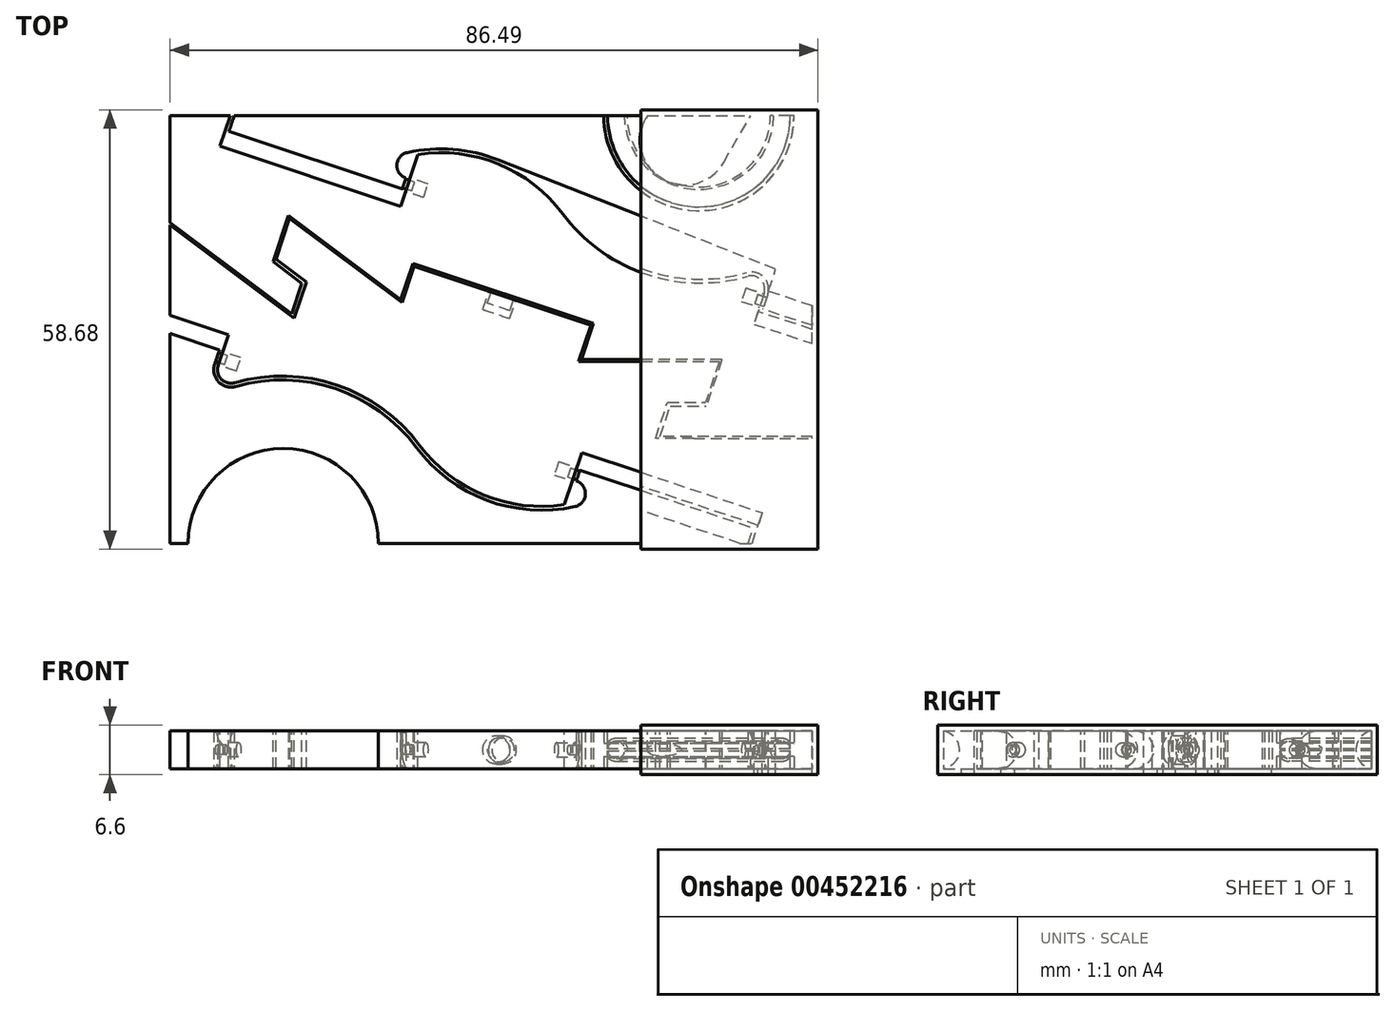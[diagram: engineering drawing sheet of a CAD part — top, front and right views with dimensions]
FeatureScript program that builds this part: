
annotation { "Feature Type Name" : "Feature", "Feature Type Description" : "" }
export const myFeature = defineFeature(function(context is Context, id is Id, definition is map)
    precondition{}
    {
        {
            var Q0;
            Q0=qCreatedBy(makeId("Top.planeOp"),FACE);
            cPlane(context, id + "F0", {"entities" : qUnion([Q0]), "cplaneType" : CPlaneType.OFFSET, "offset" : 2.54 * mm, "width" : 152.4 * mm, "height" : 152.4 * mm});
        }
        {
            var Q0;
            Q0=qCreatedBy(makeId("Top.planeOp"),FACE);
            var sketch = newSketch(context, id + "F1", { "sketchPlane" : qUnion([Q0])});
            skLineSegment(sketch, "E0", {"start": v(0, 0) * mm, "end": v(0, 28.58) * mm});
            skLineSegment(sketch, "E1", {"start": v(0, 0) * mm, "end": v(85.73, 0) * mm, "construction": true});
            skLineSegment(sketch, "E2", {"start": v(0, 28.58) * mm, "end": v(85.73, 0) * mm, "construction": true});
            skLineSegment(sketch, "E3", {"start": v(0, 28.58) * mm, "end": v(8.03, 28.58) * mm});
            skLineSegment(sketch, "E4", {"start": v(8.03, 28.58) * mm, "end": v(7.23, 26.17) * mm});
            skLineSegment(sketch, "E5", {"start": v(7.23, 26.17) * mm, "end": v(31.33, 18.13) * mm});
            skLineSegment(sketch, "E6", {"start": v(31.33, 18.13) * mm, "end": v(32.13, 20.54) * mm});
            skLineSegment(sketch, "E7", {"start": v(32.13, 20.54) * mm, "end": v(31.65, 20.7) * mm});
            skArc(sketch, "E8", {"start": v(31.78, 23.15) * mm, "mid": v(30.78, 21.98) * mm, "end": v(31.65, 20.7) * mm});
            skArc(sketch, "E9", {"start": v(52.44, 15.43) * mm, "mid": v(43.25, 22.34) * mm, "end": v(31.78, 23.15) * mm});
            skArc(sketch, "E10", {"start": v(52.44, 15.43) * mm, "mid": v(63.47, 7.42) * mm, "end": v(77.1, 7.11) * mm});
            skArc(sketch, "E11", {"start": v(79.3, 4.82) * mm, "mid": v(78.9, 6.63) * mm, "end": v(77.1, 7.11) * mm});
            skLineSegment(sketch, "E12", {"start": v(79.3, 4.82) * mm, "end": v(78.5, 2.4) * mm});
            skLineSegment(sketch, "E13", {"start": v(78.5, 2.4) * mm, "end": v(85.73, 0) * mm});
            skLineSegment(sketch, "E14", {"start": v(0, 0) * mm, "end": v(0, -28.58) * mm, "construction": true});
            skLineSegment(sketch, "E15", {"start": v(0, -28.58) * mm, "end": v(85.73, -28.58) * mm, "construction": true});
            skLineSegment(sketch, "E16", {"start": v(0, 14.29) * mm, "end": v(85.73, -14.29) * mm, "construction": true});
            skLineSegment(sketch, "E17", {"start": v(85.73, 0) * mm, "end": v(85.73, -14.29) * mm});
            skLineSegment(sketch, "E18", {"start": v(85.73, -14.29) * mm, "end": v(70.23, -14.29) * mm});
            skLineSegment(sketch, "E19", {"start": v(73.65, -4.02) * mm, "end": v(54.91, -4.02) * mm});
            skLineSegment(sketch, "E20", {"start": v(54.91, -4.02) * mm, "end": v(56.52, 0.8) * mm});
            skLineSegment(sketch, "E21", {"start": v(56.52, 0.8) * mm, "end": v(32.42, 8.84) * mm});
            skLineSegment(sketch, "E22", {"start": v(32.42, 8.84) * mm, "end": v(30.81, 4.02) * mm});
            skLineSegment(sketch, "E23", {"start": v(30.81, 4.02) * mm, "end": v(15.82, 15.26) * mm});
            skLineSegment(sketch, "E24", {"start": v(12.4, 5) * mm, "end": v(0, 14.29) * mm});
            skLineSegment(sketch, "E25", {"start": v(15.82, 15.26) * mm, "end": v(12.4, 5) * mm});
            skLineSegment(sketch, "E26", {"start": v(73.65, -4.02) * mm, "end": v(70.23, -14.29) * mm});
            skSolve(sketch);
        }
        {
            var Q0;
            Q0=qCreatedBy(makeId("Top.planeOp"),FACE);
            var sketch = newSketch(context, id + "F2", { "sketchPlane" : qUnion([Q0])});
            skLineSegment(sketch, "E27", {"start": v(85.73, 0) * mm, "end": v(85.73, -28.58) * mm, "construction": true});
            skLineSegment(sketch, "E28", {"start": v(85.73, 0) * mm, "end": v(0, 0) * mm, "construction": true});
            skLineSegment(sketch, "E29", {"start": v(85.73, -28.58) * mm, "end": v(0, 0) * mm, "construction": true});
            skLineSegment(sketch, "E30", {"start": v(85.73, -28.58) * mm, "end": v(77.7, -28.58) * mm});
            skLineSegment(sketch, "E31", {"start": v(77.7, -28.58) * mm, "end": v(78.5, -26.17) * mm});
            skLineSegment(sketch, "E32", {"start": v(78.5, -26.17) * mm, "end": v(54.4, -18.13) * mm});
            skLineSegment(sketch, "E33", {"start": v(54.4, -18.13) * mm, "end": v(53.6, -20.54) * mm});
            skLineSegment(sketch, "E34", {"start": v(53.6, -20.54) * mm, "end": v(54.08, -20.7) * mm});
            skArc(sketch, "E35", {"start": v(53.95, -23.15) * mm, "mid": v(54.94, -21.98) * mm, "end": v(54.08, -20.7) * mm});
            skArc(sketch, "E36", {"start": v(33.29, -15.43) * mm, "mid": v(42.48, -22.34) * mm, "end": v(53.95, -23.15) * mm});
            skArc(sketch, "E37", {"start": v(33.29, -15.43) * mm, "mid": v(22.26, -7.42) * mm, "end": v(8.62, -7.11) * mm});
            skArc(sketch, "E38", {"start": v(6.43, -4.82) * mm, "mid": v(6.83, -6.63) * mm, "end": v(8.62, -7.11) * mm});
            skLineSegment(sketch, "E39", {"start": v(6.43, -4.82) * mm, "end": v(7.23, -2.4) * mm});
            skLineSegment(sketch, "E40", {"start": v(7.23, -2.4) * mm, "end": v(0, 0) * mm});
            skLineSegment(sketch, "E41", {"start": v(85.73, 0) * mm, "end": v(85.73, 28.58) * mm, "construction": true});
            skLineSegment(sketch, "E42", {"start": v(85.73, 28.58) * mm, "end": v(0, 28.58) * mm, "construction": true});
            skLineSegment(sketch, "E43", {"start": v(85.73, -14.29) * mm, "end": v(0, 14.29) * mm, "construction": true});
            skLineSegment(sketch, "E44", {"start": v(0, 0) * mm, "end": v(0, 14.29) * mm, "construction": true});
            skLineSegment(sketch, "E45", {"start": v(0, 0) * mm, "end": v(0, 13.97) * mm});
            skLineSegment(sketch, "E46", {"start": v(12.53, 4.58) * mm, "end": v(15.95, 14.85) * mm});
            skLineSegment(sketch, "E47", {"start": v(15.95, 14.85) * mm, "end": v(30.94, 3.6) * mm});
            skLineSegment(sketch, "E48", {"start": v(30.94, 3.6) * mm, "end": v(32.55, 8.42) * mm});
            skLineSegment(sketch, "E49", {"start": v(32.55, 8.42) * mm, "end": v(56.16, 0.55) * mm});
            skLineSegment(sketch, "E50", {"start": v(56.16, 0.55) * mm, "end": v(54.56, -4.27) * mm});
            skLineSegment(sketch, "E51", {"start": v(54.56, -4.27) * mm, "end": v(73.3, -4.27) * mm});
            skLineSegment(sketch, "E52", {"start": v(73.3, -4.27) * mm, "end": v(69.88, -14.54) * mm});
            skLineSegment(sketch, "E53", {"start": v(69.88, -14.54) * mm, "end": v(85.73, -14.54) * mm});
            skLineSegment(sketch, "E54", {"start": v(0, 13.97) * mm, "end": v(12.53, 4.58) * mm});
            skLineSegment(sketch, "E55", {"start": v(6.26, 9.27) * mm, "end": v(6.42, 9.48) * mm, "construction": true});
            skLineSegment(sketch, "E56", {"start": v(14.24, 9.71) * mm, "end": v(14, 9.8) * mm, "construction": true});
            skLineSegment(sketch, "E57", {"start": v(71.59, -9.4) * mm, "end": v(71.83, -9.49) * mm, "construction": true});
            skLineSegment(sketch, "E58", {"start": v(77.8, -14.54) * mm, "end": v(77.8, -14.29) * mm, "construction": true});
            skLineSegment(sketch, "E59", {"start": v(85.73, -14.54) * mm, "end": v(85.73, -28.58) * mm});
            skSolve(sketch);
        }
        {
            var Q0;
            Q0=qCreatedBy(makeId("Top.planeOp"),FACE);
            var sketch = newSketch(context, id + "F3", { "sketchPlane" : qUnion([Q0])});
            skLineSegment(sketch, "E60.0", {"start": v(79.14, 2.73) * mm, "end": v(85.73, 0.54) * mm});
            skLineSegment(sketch, "E60.1", {"start": v(79.78, 4.66) * mm, "end": v(79.14, 2.73) * mm});
            skArc(sketch, "E60.2", {"start": v(79.78, 4.66) * mm, "mid": v(79.26, 6.98) * mm, "end": v(76.96, 7.6) * mm});
            skArc(sketch, "E60.3", {"start": v(52.85, 15.74) * mm, "mid": v(63.63, 7.9) * mm, "end": v(76.96, 7.6) * mm});
            skArc(sketch, "E60.4", {"start": v(52.85, 15.74) * mm, "mid": v(43.42, 22.81) * mm, "end": v(31.67, 23.64) * mm});
            skLineSegment(sketch, "E60.5", {"start": v(8.57, 28.58) * mm, "end": v(7.87, 26.49) * mm});
            skLineSegment(sketch, "E60.6", {"start": v(7.87, 26.49) * mm, "end": v(31, 18.78) * mm});
            skLineSegment(sketch, "E60.7", {"start": v(31, 18.78) * mm, "end": v(31.49, 20.22) * mm});
            skArc(sketch, "E60.8", {"start": v(31.67, 23.64) * mm, "mid": v(30.27, 22) * mm, "end": v(31.49, 20.22) * mm});
            skLineSegment(sketch, "E61", {"start": v(8.57, 28.58) * mm, "end": v(57.91, 28.58) * mm});
            skLineSegment(sketch, "E62", {"start": v(85.73, 28.58) * mm, "end": v(85.73, 0.54) * mm});
            skLineSegment(sketch, "E63", {"start": v(85.73, 28.58) * mm, "end": v(83.31, 28.58) * mm});
            skArc(sketch, "E64", {"start": v(57.91, 28.58) * mm, "mid": v(70.61, 15.88) * mm, "end": v(83.31, 28.58) * mm});
            skLineSegment(sketch, "E65", {"start": v(70.78, 29.08) * mm, "end": v(63.55, 7.4) * mm, "construction": true});
            skPoint(sketch, "E66", {"position": v(42.86, 0) * mm});
            skArc(sketch, "E67.1.0", {"start": v(54.06, -23.64) * mm, "mid": v(55.45, -22) * mm, "end": v(54.24, -20.22) * mm});
            skLineSegment(sketch, "E67.1.1", {"start": v(77.85, -26.49) * mm, "end": v(54.72, -18.78) * mm});
            skLineSegment(sketch, "E67.1.2", {"start": v(77.16, -28.58) * mm, "end": v(27.81, -28.58) * mm});
            skArc(sketch, "E67.1.3", {"start": v(32.88, -15.74) * mm, "mid": v(42.3, -22.81) * mm, "end": v(54.06, -23.64) * mm});
            skArc(sketch, "E67.1.4", {"start": v(32.88, -15.74) * mm, "mid": v(22.1, -7.9) * mm, "end": v(8.76, -7.6) * mm});
            skLineSegment(sketch, "E67.1.5", {"start": v(6.59, -2.73) * mm, "end": v(0, -0.54) * mm});
            skArc(sketch, "E67.1.6", {"start": v(27.81, -28.58) * mm, "mid": v(15.11, -15.88) * mm, "end": v(2.41, -28.58) * mm});
            skLineSegment(sketch, "E67.1.7", {"start": v(14.95, -29.08) * mm, "end": v(22.18, -7.4) * mm, "construction": true});
            skArc(sketch, "E67.1.8", {"start": v(5.94, -4.66) * mm, "mid": v(6.47, -6.98) * mm, "end": v(8.76, -7.6) * mm});
            skLineSegment(sketch, "E67.1.9", {"start": v(0, -28.58) * mm, "end": v(0, -0.54) * mm});
            skLineSegment(sketch, "E67.1.10", {"start": v(77.16, -28.58) * mm, "end": v(77.85, -26.49) * mm});
            skLineSegment(sketch, "E67.1.11", {"start": v(54.72, -18.78) * mm, "end": v(54.24, -20.22) * mm});
            skLineSegment(sketch, "E67.1.12", {"start": v(0, -28.58) * mm, "end": v(2.41, -28.58) * mm});
            skLineSegment(sketch, "E67.1.13", {"start": v(5.94, -4.66) * mm, "end": v(6.59, -2.73) * mm});
            skSolve(sketch);
        }
        {
            var Q0;
            Q0=qSketchRegion(id+"F1",true);
            extrude(context, id + "F4", {"entities" : qUnion([Q0]), "depth" : 5.08 * mm});
        }
        {
            var Q0;
            Q0=qSketchRegion(id+"F2",true);
            extrude(context, id + "F5", {"entities" : qUnion([Q0]), "depth" : 5.08 * mm});
        }
        {
            var Q0;
            Q0=qSketchRegion(id+"F3",true);
            extrude(context, id + "F6", {"entities" : qUnion([Q0]), "depth" : 5.08 * mm});
        }
        {
            var Q0;
            Q0=makeQuery(id+"F4.opExtrude","SWEPT_FACE",FACE,{"disambiguationData":[OSD([sQuery(id+"F1.wireOp",EDGE,"E6")])]});
            var sketch = newSketch(context, id + "F7", { "sketchPlane" : qUnion([Q0])});
            skCircle(sketch, "E68", {"center": v(-28.38, 2.54) * mm, "radius": 0.95 * mm});
            skLineSegment(sketch, "E69.bottom", {"start": v(-29.65, 5.08) * mm, "end": v(-27.1, 5.08) * mm, "construction": true});
            skLineSegment(sketch, "E69.top", {"start": v(-29.65, 0) * mm, "end": v(-27.1, 0) * mm, "construction": true});
            skLineSegment(sketch, "E69.left", {"start": v(-29.65, 5.08) * mm, "end": v(-29.65, 0) * mm, "construction": true});
            skLineSegment(sketch, "E69.right", {"start": v(-27.1, 5.08) * mm, "end": v(-27.1, 0) * mm, "construction": true});
            skLineSegment(sketch, "E70", {"start": v(-29.65, 2.54) * mm, "end": v(-27.1, 2.54) * mm, "construction": true});
            skSolve(sketch);
        }
        {
            var Q0;
            Q0=qSketchRegion(id+"F7",true);
            extrude(context, id + "F8", {"entities" : qUnion([Q0]), "operationType" : NewBodyOperationType.REMOVE, "oppositeDirection" : true, "depth" : 2.54 * mm});
        }
        {
            var Q0;
            Q0=makeQuery(id+"F6.opExtrude","SWEPT_FACE",FACE,{"disambiguationData":[OSD([sQuery(id+"F3.wireOp",EDGE,"E60.7")])]});
            var sketch = newSketch(context, id + "F9", { "sketchPlane" : qUnion([Q0])});
            skLineSegment(sketch, "E71", {"start": v(29.14, 5.08) * mm, "end": v(29.14, 0) * mm, "construction": true});
            skLineSegment(sketch, "E72", {"start": v(29.14, 0) * mm, "end": v(27.62, 0) * mm, "construction": true});
            skLineSegment(sketch, "E73", {"start": v(27.62, 0) * mm, "end": v(27.62, 5.08) * mm, "construction": true});
            skLineSegment(sketch, "E74", {"start": v(27.62, 5.08) * mm, "end": v(29.14, 5.08) * mm, "construction": true});
            skCircle(sketch, "E75", {"center": v(28.38, 2.54) * mm, "radius": 0.64 * mm});
            skLineSegment(sketch, "E76", {"start": v(29.14, 2.54) * mm, "end": v(27.62, 2.54) * mm, "construction": true});
            skSolve(sketch);
        }
        {
            var Q0;
            Q0=qSketchRegion(id+"F9",true);
            extrude(context, id + "F10", {"entities" : qUnion([Q0]), "operationType" : NewBodyOperationType.ADD, "depth" : 1.27 * mm});
        }
        {
            var Q0;
            Q0=makeQuery(id+"F6.opExtrude","SWEPT_FACE",FACE,{"disambiguationData":[OSD([sQuery(id+"F3.wireOp",EDGE,"E60.1")])]});
            var sketch = newSketch(context, id + "F11", { "sketchPlane" : qUnion([Q0])});
            skLineSegment(sketch, "E77.bottom", {"start": v(-29.65, 5.08) * mm, "end": v(-27.62, 5.08) * mm, "construction": true});
            skLineSegment(sketch, "E77.top", {"start": v(-29.65, 0) * mm, "end": v(-27.62, 0) * mm, "construction": true});
            skLineSegment(sketch, "E77.left", {"start": v(-29.65, 5.08) * mm, "end": v(-29.65, 0) * mm, "construction": true});
            skLineSegment(sketch, "E77.right", {"start": v(-27.62, 5.08) * mm, "end": v(-27.62, 0) * mm, "construction": true});
            skLineSegment(sketch, "E78", {"start": v(-29.65, 2.54) * mm, "end": v(-27.62, 2.54) * mm, "construction": true});
            skCircle(sketch, "E79", {"center": v(-28.63, 2.54) * mm, "radius": 0.64 * mm});
            skSolve(sketch);
        }
        {
            var Q0;
            Q0=makeQuery(id+"F4.opExtrude","SWEPT_FACE",FACE,{"disambiguationData":[OSD([sQuery(id+"F1.wireOp",EDGE,"E12")])]});
            var sketch = newSketch(context, id + "F12", { "sketchPlane" : qUnion([Q0])});
            skLineSegment(sketch, "E80.bottom", {"start": v(29.65, 5.08) * mm, "end": v(27.62, 5.08) * mm, "construction": true});
            skLineSegment(sketch, "E80.top", {"start": v(29.65, 0) * mm, "end": v(27.62, 0) * mm, "construction": true});
            skLineSegment(sketch, "E80.left", {"start": v(29.65, 5.08) * mm, "end": v(29.65, 0) * mm, "construction": true});
            skLineSegment(sketch, "E80.right", {"start": v(27.62, 5.08) * mm, "end": v(27.62, 0) * mm, "construction": true});
            skLineSegment(sketch, "E81", {"start": v(29.65, 2.54) * mm, "end": v(27.62, 2.54) * mm, "construction": true});
            skCircle(sketch, "E82", {"center": v(28.63, 2.54) * mm, "radius": 0.95 * mm});
            skSolve(sketch);
        }
        {
            var Q0;
            Q0=qSketchRegion(id+"F12",true);
            extrude(context, id + "F13", {"entities" : qUnion([Q0]), "operationType" : NewBodyOperationType.REMOVE, "oppositeDirection" : true, "depth" : 2.54 * mm});
        }
        {
            var Q0;
            Q0=qSketchRegion(id+"F11",true);
            extrude(context, id + "F14", {"entities" : qUnion([Q0]), "operationType" : NewBodyOperationType.ADD, "depth" : 1.27 * mm});
        }
        {
            var Q0;
            Q0=makeQuery(id+"F4.opExtrude","SWEPT_FACE",FACE,{"disambiguationData":[OSD([sQuery(id+"F1.wireOp",EDGE,"E21")])]});
            var sketch = newSketch(context, id + "F15", { "sketchPlane" : qUnion([Q0])});
            skLineSegment(sketch, "E83.bottom", {"start": v(27.96, 5.08) * mm, "end": v(53.36, 5.08) * mm, "construction": true});
            skLineSegment(sketch, "E83.top", {"start": v(27.96, 0) * mm, "end": v(53.36, 0) * mm, "construction": true});
            skLineSegment(sketch, "E83.left", {"start": v(27.96, 5.08) * mm, "end": v(27.96, 0) * mm, "construction": true});
            skLineSegment(sketch, "E83.right", {"start": v(53.36, 5.08) * mm, "end": v(53.36, 0) * mm, "construction": true});
            skLineSegment(sketch, "E84", {"start": v(40.66, 5.08) * mm, "end": v(40.66, 0) * mm, "construction": true});
            skCircle(sketch, "E85", {"center": v(40.66, 2.54) * mm, "radius": 1.59 * mm});
            skSolve(sketch);
        }
        {
            var Q0;
            Q0=makeQuery(id+"F5.opExtrude","SWEPT_FACE",FACE,{"disambiguationData":[OSD([sQuery(id+"F2.wireOp",EDGE,"E49")])]});
            var sketch = newSketch(context, id + "F16", { "sketchPlane" : qUnion([Q0])});
            skLineSegment(sketch, "E86.bottom", {"start": v(-53.1, 5.08) * mm, "end": v(-28.22, 5.08) * mm, "construction": true});
            skLineSegment(sketch, "E86.top", {"start": v(-53.1, 0) * mm, "end": v(-28.22, 0) * mm, "construction": true});
            skLineSegment(sketch, "E86.left", {"start": v(-53.1, 5.08) * mm, "end": v(-53.1, 0) * mm, "construction": true});
            skLineSegment(sketch, "E86.right", {"start": v(-28.22, 5.08) * mm, "end": v(-28.22, 0) * mm, "construction": true});
            skLineSegment(sketch, "E87", {"start": v(-40.66, 5.08) * mm, "end": v(-40.66, 0) * mm, "construction": true});
            skCircle(sketch, "E88", {"center": v(-40.66, 2.54) * mm, "radius": 1.9 * mm});
            skSolve(sketch);
        }
        {
            var Q0;
            Q0=qSketchRegion(id+"F16",true);
            extrude(context, id + "F17", {"entities" : qUnion([Q0]), "operationType" : NewBodyOperationType.REMOVE, "oppositeDirection" : true, "depth" : 2.54 * mm});
        }
        {
            var Q0;
            Q0=qSketchRegion(id+"F15",true);
            extrude(context, id + "F18", {"entities" : qUnion([Q0]), "operationType" : NewBodyOperationType.ADD, "depth" : 1.9 * mm});
        }
        {
            var Q0;
            Q0=makeQuery(id+"F5.opExtrude","CAP_FACE",FACE,{"disambiguationData":[OSD([sQuery(id+"F2.wireOp",EDGE,"E30"),sQuery(id+"F2.wireOp",EDGE,"E31"),sQuery(id+"F2.wireOp",EDGE,"E32"),sQuery(id+"F2.wireOp",EDGE,"E33"),sQuery(id+"F2.wireOp",EDGE,"E34"),sQuery(id+"F2.wireOp",EDGE,"E35"),sQuery(id+"F2.wireOp",EDGE,"E36"),sQuery(id+"F2.wireOp",EDGE,"E37"),sQuery(id+"F2.wireOp",EDGE,"E38"),sQuery(id+"F2.wireOp",EDGE,"E39"),sQuery(id+"F2.wireOp",EDGE,"E40"),sQuery(id+"F2.wireOp",EDGE,"E45"),sQuery(id+"F2.wireOp",EDGE,"E46"),sQuery(id+"F2.wireOp",EDGE,"E47"),sQuery(id+"F2.wireOp",EDGE,"E48"),sQuery(id+"F2.wireOp",EDGE,"E49"),sQuery(id+"F2.wireOp",EDGE,"E50"),sQuery(id+"F2.wireOp",EDGE,"E51"),sQuery(id+"F2.wireOp",EDGE,"E52"),sQuery(id+"F2.wireOp",EDGE,"E53"),sQuery(id+"F2.wireOp",EDGE,"E54"),sQuery(id+"F2.wireOp",EDGE,"E59")])],"isStart":false});
            var sketch = newSketch(context, id + "F19", { "sketchPlane" : qUnion([Q0])});
            skLineSegment(sketch, "E89", {"start": v(12.53, 4.58) * mm, "end": v(16.6, 1.53) * mm});
            skLineSegment(sketch, "E90", {"start": v(16.6, 1.53) * mm, "end": v(18.2, 6.35) * mm});
            skLineSegment(sketch, "E91", {"start": v(18.2, 6.35) * mm, "end": v(14.13, 9.4) * mm});
            skLineSegment(sketch, "E92", {"start": v(14.13, 9.4) * mm, "end": v(12.53, 4.58) * mm});
            skLineSegment(sketch, "E93", {"start": v(44.36, 4.49) * mm, "end": v(44.64, 5.33) * mm, "construction": true});
            skLineSegment(sketch, "E94.MirrorCS", {"start": v(69.88, -14.54) * mm, "end": v(64.8, -14.54) * mm});
            skLineSegment(sketch, "E95.MirrorCS", {"start": v(64.8, -14.54) * mm, "end": v(66.4, -9.72) * mm});
            skLineSegment(sketch, "E96.MirrorCS", {"start": v(66.4, -9.72) * mm, "end": v(71.48, -9.72) * mm});
            skLineSegment(sketch, "E97.MirrorCS", {"start": v(71.48, -9.72) * mm, "end": v(69.88, -14.54) * mm});
            skSolve(sketch);
        }
        {
            var Q0;
            Q0=qSketchRegion(id+"F19",true);
            extrude(context, id + "F20", {"entities" : qUnion([Q0]), "operationType" : NewBodyOperationType.REMOVE, "endBound" : BoundingType.THROUGH_ALL, "oppositeDirection" : true, "depth" : 25.4 * mm});
        }
        {
            var Q0;
            Q0=makeQuery(id+"F4.opExtrude","CAP_FACE",FACE,{"disambiguationData":[OSD([sQuery(id+"F1.wireOp",EDGE,"E0"),sQuery(id+"F1.wireOp",EDGE,"E3"),sQuery(id+"F1.wireOp",EDGE,"E4"),sQuery(id+"F1.wireOp",EDGE,"E5"),sQuery(id+"F1.wireOp",EDGE,"E6"),sQuery(id+"F1.wireOp",EDGE,"E7"),sQuery(id+"F1.wireOp",EDGE,"E8"),sQuery(id+"F1.wireOp",EDGE,"E9"),sQuery(id+"F1.wireOp",EDGE,"E10"),sQuery(id+"F1.wireOp",EDGE,"E11"),sQuery(id+"F1.wireOp",EDGE,"E12"),sQuery(id+"F1.wireOp",EDGE,"E13"),sQuery(id+"F1.wireOp",EDGE,"E17"),sQuery(id+"F1.wireOp",EDGE,"E18"),sQuery(id+"F1.wireOp",EDGE,"E19"),sQuery(id+"F1.wireOp",EDGE,"E20"),sQuery(id+"F1.wireOp",EDGE,"E21"),sQuery(id+"F1.wireOp",EDGE,"E22"),sQuery(id+"F1.wireOp",EDGE,"E23"),sQuery(id+"F1.wireOp",EDGE,"E24"),sQuery(id+"F1.wireOp",EDGE,"E25"),sQuery(id+"F1.wireOp",EDGE,"E26")])],"isStart":false});
            var sketch = newSketch(context, id + "F21", { "sketchPlane" : qUnion([Q0])});
            skLineSegment(sketch, "E98", {"start": v(13.75, 9.05) * mm, "end": v(17.6, 6.16) * mm});
            skLineSegment(sketch, "E99", {"start": v(17.6, 6.16) * mm, "end": v(16.25, 2.1) * mm});
            skLineSegment(sketch, "E100", {"start": v(16.25, 2.1) * mm, "end": v(12.4, 5) * mm});
            skLineSegment(sketch, "E101", {"start": v(12.4, 5) * mm, "end": v(13.75, 9.05) * mm});
            skLineSegment(sketch, "E102", {"start": v(71.58, -10.23) * mm, "end": v(66.77, -10.23) * mm});
            skLineSegment(sketch, "E103", {"start": v(66.77, -10.23) * mm, "end": v(65.42, -14.29) * mm});
            skLineSegment(sketch, "E104", {"start": v(65.42, -14.29) * mm, "end": v(70.23, -14.29) * mm});
            skLineSegment(sketch, "E105", {"start": v(70.23, -14.29) * mm, "end": v(71.58, -10.23) * mm});
            skSolve(sketch);
        }
        {
            var Q0;
            Q0=qSketchRegion(id+"F21",true);
            var Q1;
            Q1=makeQuery(id+"F4.opExtrude","CAP_FACE",FACE,{"disambiguationData":[OSD([sQuery(id+"F1.wireOp",EDGE,"E0"),sQuery(id+"F1.wireOp",EDGE,"E3"),sQuery(id+"F1.wireOp",EDGE,"E4"),sQuery(id+"F1.wireOp",EDGE,"E5"),sQuery(id+"F1.wireOp",EDGE,"E6"),sQuery(id+"F1.wireOp",EDGE,"E7"),sQuery(id+"F1.wireOp",EDGE,"E8"),sQuery(id+"F1.wireOp",EDGE,"E9"),sQuery(id+"F1.wireOp",EDGE,"E10"),sQuery(id+"F1.wireOp",EDGE,"E11"),sQuery(id+"F1.wireOp",EDGE,"E12"),sQuery(id+"F1.wireOp",EDGE,"E13"),sQuery(id+"F1.wireOp",EDGE,"E17"),sQuery(id+"F1.wireOp",EDGE,"E18"),sQuery(id+"F1.wireOp",EDGE,"E19"),sQuery(id+"F1.wireOp",EDGE,"E20"),sQuery(id+"F1.wireOp",EDGE,"E21"),sQuery(id+"F1.wireOp",EDGE,"E22"),sQuery(id+"F1.wireOp",EDGE,"E23"),sQuery(id+"F1.wireOp",EDGE,"E24"),sQuery(id+"F1.wireOp",EDGE,"E25"),sQuery(id+"F1.wireOp",EDGE,"E26")])],"isStart":true});
            extrude(context, id + "F22", {"entities" : qUnion([Q0]), "operationType" : NewBodyOperationType.ADD, "endBound" : BoundingType.UP_TO_SURFACE, "oppositeDirection" : true, "endBoundEntityFace" : qUnion([Q1]), "depth" : 25.4 * mm});
        }
        {
            var Q0;
            Q0=makeQuery(id+"F5.opExtrude","SWEPT_FACE",FACE,{"disambiguationData":[OSD([sQuery(id+"F2.wireOp",EDGE,"E33")])]});
            var sketch = newSketch(context, id + "F23", { "sketchPlane" : qUnion([Q0])});
            skLineSegment(sketch, "E106.bottom", {"start": v(0, 5.08) * mm, "end": v(-2.54, 5.08) * mm, "construction": true});
            skLineSegment(sketch, "E106.top", {"start": v(0, 0) * mm, "end": v(-2.54, 0) * mm, "construction": true});
            skLineSegment(sketch, "E106.left", {"start": v(0, 5.08) * mm, "end": v(0, 0) * mm, "construction": true});
            skLineSegment(sketch, "E106.right", {"start": v(-2.54, 5.08) * mm, "end": v(-2.54, 0) * mm, "construction": true});
            skLineSegment(sketch, "E107", {"start": v(0, 2.54) * mm, "end": v(-2.54, 2.54) * mm, "construction": true});
            skCircle(sketch, "E108", {"center": v(-1.27, 2.54) * mm, "radius": 0.95 * mm});
            skSolve(sketch);
        }
        {
            var Q0;
            Q0=makeQuery(id+"F6.opExtrude","SWEPT_FACE",FACE,{"disambiguationData":[OSD([sQuery(id+"F3.wireOp",EDGE,"E67.1.11")])]});
            var sketch = newSketch(context, id + "F24", { "sketchPlane" : qUnion([Q0])});
            skLineSegment(sketch, "E109.bottom", {"start": v(2.03, 0) * mm, "end": v(0.5, 0) * mm, "construction": true});
            skLineSegment(sketch, "E109.top", {"start": v(2.03, 5.08) * mm, "end": v(0.5, 5.08) * mm, "construction": true});
            skLineSegment(sketch, "E109.left", {"start": v(2.03, 0) * mm, "end": v(2.03, 5.08) * mm, "construction": true});
            skLineSegment(sketch, "E109.right", {"start": v(0.5, 0) * mm, "end": v(0.5, 5.08) * mm, "construction": true});
            skLineSegment(sketch, "E110", {"start": v(0.5, 2.54) * mm, "end": v(2.03, 2.54) * mm, "construction": true});
            skCircle(sketch, "E111", {"center": v(1.27, 2.54) * mm, "radius": 0.64 * mm});
            skSolve(sketch);
        }
        {
            var Q0;
            Q0=qSketchRegion(id+"F23",true);
            extrude(context, id + "F25", {"entities" : qUnion([Q0]), "operationType" : NewBodyOperationType.REMOVE, "oppositeDirection" : true, "depth" : 2.54 * mm});
        }
        {
            var Q0;
            Q0=qSketchRegion(id+"F24",true);
            extrude(context, id + "F26", {"entities" : qUnion([Q0]), "operationType" : NewBodyOperationType.ADD, "depth" : 1.27 * mm});
        }
        {
            var Q0;
            Q0=makeQuery(id+"F6.opExtrude","SWEPT_FACE",FACE,{"disambiguationData":[OSD([sQuery(id+"F3.wireOp",EDGE,"E67.1.13")])]});
            var sketch = newSketch(context, id + "F27", { "sketchPlane" : qUnion([Q0])});
            skLineSegment(sketch, "E112.bottom", {"start": v(-0.5, 5.08) * mm, "end": v(-2.54, 5.08) * mm, "construction": true});
            skLineSegment(sketch, "E112.top", {"start": v(-0.5, 0) * mm, "end": v(-2.54, 0) * mm, "construction": true});
            skLineSegment(sketch, "E112.left", {"start": v(-0.5, 5.08) * mm, "end": v(-0.5, 0) * mm, "construction": true});
            skLineSegment(sketch, "E112.right", {"start": v(-2.54, 5.08) * mm, "end": v(-2.54, 0) * mm, "construction": true});
            skLineSegment(sketch, "E113", {"start": v(-0.5, 2.54) * mm, "end": v(-2.54, 2.54) * mm, "construction": true});
            skCircle(sketch, "E114", {"center": v(-1.52, 2.54) * mm, "radius": 0.64 * mm});
            skSolve(sketch);
        }
        {
            var Q0;
            Q0=makeQuery(id+"F5.opExtrude","SWEPT_FACE",FACE,{"disambiguationData":[OSD([sQuery(id+"F2.wireOp",EDGE,"E39")])]});
            var sketch = newSketch(context, id + "F28", { "sketchPlane" : qUnion([Q0])});
            skLineSegment(sketch, "E115.bottom", {"start": v(0.5, 0) * mm, "end": v(2.54, 0) * mm, "construction": true});
            skLineSegment(sketch, "E115.top", {"start": v(0.5, 5.08) * mm, "end": v(2.54, 5.08) * mm, "construction": true});
            skLineSegment(sketch, "E115.left", {"start": v(0.5, 0) * mm, "end": v(0.5, 5.08) * mm, "construction": true});
            skLineSegment(sketch, "E115.right", {"start": v(2.54, 0) * mm, "end": v(2.54, 5.08) * mm, "construction": true});
            skLineSegment(sketch, "E116", {"start": v(0.5, 2.54) * mm, "end": v(2.54, 2.54) * mm, "construction": true});
            skCircle(sketch, "E117", {"center": v(1.52, 2.54) * mm, "radius": 0.95 * mm});
            skSolve(sketch);
        }
        {
            var Q0;
            Q0=qSketchRegion(id+"F28",true);
            extrude(context, id + "F29", {"entities" : qUnion([Q0]), "operationType" : NewBodyOperationType.REMOVE, "oppositeDirection" : true, "depth" : 2.54 * mm});
        }
        {
            var Q0;
            Q0=qSketchRegion(id+"F27",true);
            extrude(context, id + "F30", {"entities" : qUnion([Q0]), "operationType" : NewBodyOperationType.ADD, "depth" : 1.27 * mm});
        }
        {
            var Q0;
            Q0=qCreatedBy(id+"F0.planeOp",FACE);
            var sketch = newSketch(context, id + "F31", { "sketchPlane" : qUnion([Q0])});
            skArc(sketch, "E118", {"start": v(57.91, 28.58) * mm, "mid": v(70.61, 15.88) * mm, "end": v(83.31, 28.58) * mm});
            skLineSegment(sketch, "E119", {"start": v(57.91, 28.58) * mm, "end": v(58.93, 28.58) * mm});
            skLineSegment(sketch, "E120", {"start": v(83.31, 28.58) * mm, "end": v(82.3, 28.58) * mm});
            skArc(sketch, "E121", {"start": v(58.93, 28.58) * mm, "mid": v(70.61, 16.9) * mm, "end": v(82.3, 28.58) * mm});
            skSolve(sketch);
        }
        {
            var Q0;
            Q0=qSketchRegion(id+"F31",true);
            extrude(context, id + "F32", {"entities" : qUnion([Q0]), "operationType" : NewBodyOperationType.ADD, "depth" : 0.89 * mm, "hasSecondDirection" : true, "secondDirectionOppositeDirection" : true, "secondDirectionDepth" : 0.89 * mm});
        }
        {
            var Q0;
            Q0=makeQuery(id+"F6.opExtrude","CAP_FACE",FACE,{"disambiguationData":[OSD([sQuery(id+"F3.wireOp",EDGE,"E60.0"),sQuery(id+"F3.wireOp",EDGE,"E60.1"),sQuery(id+"F3.wireOp",EDGE,"E60.2"),sQuery(id+"F3.wireOp",EDGE,"E60.3"),sQuery(id+"F3.wireOp",EDGE,"E60.4"),sQuery(id+"F3.wireOp",EDGE,"E60.5"),sQuery(id+"F3.wireOp",EDGE,"E60.6"),sQuery(id+"F3.wireOp",EDGE,"E60.7"),sQuery(id+"F3.wireOp",EDGE,"E60.8"),sQuery(id+"F3.wireOp",EDGE,"E61"),sQuery(id+"F3.wireOp",EDGE,"E62"),sQuery(id+"F3.wireOp",EDGE,"E63"),sQuery(id+"F3.wireOp",EDGE,"E64")])],"isStart":false});
            var sketch = newSketch(context, id + "F33", { "sketchPlane" : qUnion([Q0])});
            skArc(sketch, "E122", {"start": v(58.42, 28.58) * mm, "mid": v(70.61, 16.38) * mm, "end": v(82.8, 28.58) * mm});
            skLineSegment(sketch, "E123", {"start": v(58.42, 28.58) * mm, "end": v(63.72, 28.58) * mm});
            skLineSegment(sketch, "E124", {"start": v(63.72, 28.58) * mm, "end": v(63.54, 28.26) * mm});
            skArc(sketch, "E125", {"start": v(63.54, 28.26) * mm, "mid": v(65.72, 20.1) * mm, "end": v(73.87, 22.3) * mm});
            skLineSegment(sketch, "E126", {"start": v(73.87, 22.3) * mm, "end": v(77.5, 28.58) * mm});
            skLineSegment(sketch, "E127", {"start": v(77.5, 28.58) * mm, "end": v(82.8, 28.58) * mm});
            skLineSegment(sketch, "E128", {"start": v(70.61, 28.58) * mm, "end": v(68.7, 25.28) * mm, "construction": true});
            skSolve(sketch);
        }
        {
            var Q0;
            Q0=qSketchRegion(id+"F33",true);
            var Q1;
            Q1=makeQuery(id+"F6.opExtrude","CAP_FACE",FACE,{"disambiguationData":[OSD([sQuery(id+"F3.wireOp",EDGE,"E60.0"),sQuery(id+"F3.wireOp",EDGE,"E60.1"),sQuery(id+"F3.wireOp",EDGE,"E60.2"),sQuery(id+"F3.wireOp",EDGE,"E60.3"),sQuery(id+"F3.wireOp",EDGE,"E60.4"),sQuery(id+"F3.wireOp",EDGE,"E60.5"),sQuery(id+"F3.wireOp",EDGE,"E60.6"),sQuery(id+"F3.wireOp",EDGE,"E60.7"),sQuery(id+"F3.wireOp",EDGE,"E60.8"),sQuery(id+"F3.wireOp",EDGE,"E61"),sQuery(id+"F3.wireOp",EDGE,"E62"),sQuery(id+"F3.wireOp",EDGE,"E63"),sQuery(id+"F3.wireOp",EDGE,"E64")])],"isStart":true});
            extrude(context, id + "F34", {"entities" : qUnion([Q0]), "endBound" : BoundingType.UP_TO_SURFACE, "oppositeDirection" : true, "endBoundEntityFace" : qUnion([Q1]), "depth" : 25.4 * mm});
        }
        {
            var Q0;
            Q0=makeQuery(id+"F34.opExtrude","SWEPT_FACE",FACE,{"disambiguationData":[OSD([sQuery(id+"F33.wireOp",EDGE,"E123")])]});
            var sketch = newSketch(context, id + "F35", { "sketchPlane" : qUnion([Q0])});
            skLineSegment(sketch, "E129", {"start": v(-58.42, 2.54) * mm, "end": v(-82.8, 2.54) * mm, "construction": true});
            skLineSegment(sketch, "E130", {"start": v(-70.61, 2.54) * mm, "end": v(-70.61, 12.73) * mm, "construction": true});
            skArc(sketch, "E131", {"start": v(-58.42, 3.56) * mm, "mid": v(-61.08, 2.54) * mm, "end": v(-58.42, 1.52) * mm});
            skLineSegment(sketch, "E132", {"start": v(-58.42, 3.56) * mm, "end": v(-58.42, 1.52) * mm});
            skSolve(sketch);
        }
        {
            var Q0;
            Q0=qSketchRegion(id+"F35",true);
            var Q1;
            Q1=sQuery(id+"F35.wireOp",EDGE,"E130");
            revolve(context, id + "F36", {"operationType" : NewBodyOperationType.REMOVE, "entities" : qUnion([Q0]), "axis" : qUnion([Q1]), "revolveType" : RevolveType.FULL, "oppositeDirection" : true});
        }
        {
            var Q0;
            Q0=makeQuery(id+"F32.boolean.opBoolean","MERGE",FACE,{"derivedFrom":[makeQuery(id+"F6.opExtrude","SWEPT_FACE",FACE,{"disambiguationData":[OSD([sQuery(id+"F3.wireOp",EDGE,"E61")])]}),makeQuery(id+"F32.opExtrude","SWEPT_FACE",FACE,{"disambiguationData":[OSD([sQuery(id+"F31.wireOp",EDGE,"E119")])]})]});
            var sketch = newSketch(context, id + "F37", { "sketchPlane" : qUnion([Q0])});
            skCircle(sketch, "E133", {"center": v(-59.55, 2.54) * mm, "radius": 1.14 * mm});
            skLineSegment(sketch, "E134", {"start": v(-57.91, 5.08) * mm, "end": v(-83.31, 5.08) * mm, "construction": true});
            skLineSegment(sketch, "E135", {"start": v(-70.61, 5.08) * mm, "end": v(-70.61, -1.36) * mm, "construction": true});
            skSolve(sketch);
        }
        {
            var Q0;
            Q0=qSketchRegion(id+"F37",true);
            var Q1;
            Q1=sQuery(id+"F37.wireOp",EDGE,"E135");
            revolve(context, id + "F38", {"operationType" : NewBodyOperationType.ADD, "entities" : qUnion([Q0]), "axis" : qUnion([Q1]), "revolveType" : RevolveType.ONE_DIRECTION, "oppositeDirection" : true, "angle" : 180 * degree});
        }
        {
            var Q0;
            Q0=makeQuery(id+"F6.opExtrude","CAP_EDGE",EDGE,{"disambiguationData":[OSD([sQuery(id+"F3.wireOp",EDGE,"E60.0")])],"isStart":false});
            var Q1;
            Q1=makeQuery(id+"F6.opExtrude","CAP_EDGE",EDGE,{"disambiguationData":[OSD([sQuery(id+"F3.wireOp",EDGE,"E60.0")])],"isStart":true});
            var Q2;
            Q2=makeQuery(id+"F6.opExtrude","CAP_EDGE",EDGE,{"disambiguationData":[OSD([sQuery(id+"F3.wireOp",EDGE,"E60.6")])],"isStart":true});
            var Q3;
            Q3=makeQuery(id+"F6.opExtrude","CAP_EDGE",EDGE,{"disambiguationData":[OSD([sQuery(id+"F3.wireOp",EDGE,"E60.6")])],"isStart":false});
            var Q4;
            Q4=makeQuery(id+"F6.opExtrude","CAP_EDGE",EDGE,{"disambiguationData":[OSD([sQuery(id+"F3.wireOp",EDGE,"E67.1.1")])],"isStart":false});
            var Q5;
            Q5=makeQuery(id+"F6.opExtrude","CAP_EDGE",EDGE,{"disambiguationData":[OSD([sQuery(id+"F3.wireOp",EDGE,"E67.1.1")])],"isStart":true});
            var Q6;
            Q6=makeQuery(id+"F6.opExtrude","CAP_EDGE",EDGE,{"disambiguationData":[OSD([sQuery(id+"F3.wireOp",EDGE,"E67.1.5")])],"isStart":true});
            var Q7;
            Q7=makeQuery(id+"F6.opExtrude","CAP_EDGE",EDGE,{"disambiguationData":[OSD([sQuery(id+"F3.wireOp",EDGE,"E67.1.5")])],"isStart":false});
            fillet(context, id + "F39", {"entities" : qUnion([Q0, Q1, Q2, Q3, Q4, Q5, Q6, Q7]), "radius" : 2.54 * mm, "tangentPropagation" : true, "allowEdgeOverflow" : false});
        }
        {
            var Q0;
            Q0=makeQuery(id+"F6.opExtrude","SWEPT_FACE",FACE,{"disambiguationData":[OSD([sQuery(id+"F3.wireOp",EDGE,"E62")])]});
            var sketch = newSketch(context, id + "F40", { "sketchPlane" : qUnion([Q0])});
            skLineSegment(sketch, "E136.bottom", {"start": v(-29.34, 5.84) * mm, "end": v(29.34, 5.84) * mm});
            skLineSegment(sketch, "E136.top", {"start": v(-29.34, -0.76) * mm, "end": v(29.34, -0.76) * mm});
            skLineSegment(sketch, "E136.left", {"start": v(-29.34, 5.84) * mm, "end": v(-29.34, -0.76) * mm});
            skLineSegment(sketch, "E136.right", {"start": v(29.34, 5.84) * mm, "end": v(29.34, -0.76) * mm});
            skSolve(sketch);
        }
        {
            var Q0;
            Q0=qSketchRegion(id+"F40",true);
            extrude(context, id + "F41", {"entities" : qUnion([Q0]), "depth" : 0.76 * mm});
        }
        {
            var Q0;
            Q0=makeQuery(id+"F41.opExtrude","CAP_FACE",FACE,{"disambiguationData":[OSD([sQuery(id+"F40.wireOp",EDGE,"E136.bottom"),sQuery(id+"F40.wireOp",EDGE,"E136.top"),sQuery(id+"F40.wireOp",EDGE,"E136.left"),sQuery(id+"F40.wireOp",EDGE,"E136.right")])],"isStart":true});
            var sketch = newSketch(context, id + "F42", { "sketchPlane" : qUnion([Q0])});
            skLineSegment(sketch, "E137.bottom", {"start": v(29.34, 5.84) * mm, "end": v(-29.34, 5.84) * mm});
            skLineSegment(sketch, "E137.top", {"start": v(29.34, -0.76) * mm, "end": v(-29.34, -0.76) * mm});
            skLineSegment(sketch, "E137.left", {"start": v(29.34, 5.84) * mm, "end": v(29.34, -0.76) * mm});
            skLineSegment(sketch, "E137.right", {"start": v(-29.34, 5.84) * mm, "end": v(-29.34, -0.76) * mm});
            skLineSegment(sketch, "E138.bottom", {"start": v(28.58, 5.08) * mm, "end": v(-28.58, 5.08) * mm});
            skLineSegment(sketch, "E138.top", {"start": v(28.58, 0) * mm, "end": v(-28.58, 0) * mm});
            skLineSegment(sketch, "E138.left", {"start": v(28.58, 5.08) * mm, "end": v(28.58, 0) * mm});
            skLineSegment(sketch, "E138.right", {"start": v(-28.58, 5.08) * mm, "end": v(-28.58, 0) * mm});
            skSolve(sketch);
        }
        {
            var Q0;
            Q0=qSketchRegion(id+"F42",true);
            extrude(context, id + "F43", {"entities" : qUnion([Q0]), "operationType" : NewBodyOperationType.ADD, "depth" : 22.86 * mm});
        }
        {
            var Q0;
            Q0=makeQuery(id+"F22.boolean.opBoolean","MERGE",FACE,{"derivedFrom":[makeQuery(id+"F4.opExtrude","CAP_FACE",FACE,{"disambiguationData":[OSD([sQuery(id+"F1.wireOp",EDGE,"E0"),sQuery(id+"F1.wireOp",EDGE,"E3"),sQuery(id+"F1.wireOp",EDGE,"E4"),sQuery(id+"F1.wireOp",EDGE,"E5"),sQuery(id+"F1.wireOp",EDGE,"E6"),sQuery(id+"F1.wireOp",EDGE,"E7"),sQuery(id+"F1.wireOp",EDGE,"E8"),sQuery(id+"F1.wireOp",EDGE,"E9"),sQuery(id+"F1.wireOp",EDGE,"E10"),sQuery(id+"F1.wireOp",EDGE,"E11"),sQuery(id+"F1.wireOp",EDGE,"E12"),sQuery(id+"F1.wireOp",EDGE,"E13"),sQuery(id+"F1.wireOp",EDGE,"E17"),sQuery(id+"F1.wireOp",EDGE,"E18"),sQuery(id+"F1.wireOp",EDGE,"E19"),sQuery(id+"F1.wireOp",EDGE,"E20"),sQuery(id+"F1.wireOp",EDGE,"E21"),sQuery(id+"F1.wireOp",EDGE,"E22"),sQuery(id+"F1.wireOp",EDGE,"E23"),sQuery(id+"F1.wireOp",EDGE,"E24"),sQuery(id+"F1.wireOp",EDGE,"E25"),sQuery(id+"F1.wireOp",EDGE,"E26")])],"isStart":false}),makeQuery(id+"F22.opExtrude","CAP_FACE",FACE,{"disambiguationData":[OSD([sQuery(id+"F21.wireOp",EDGE,"E98"),sQuery(id+"F21.wireOp",EDGE,"E99"),sQuery(id+"F21.wireOp",EDGE,"E100"),sQuery(id+"F21.wireOp",EDGE,"E101")])],"isStart":true}),makeQuery(id+"F22.opExtrude","CAP_FACE",FACE,{"disambiguationData":[OSD([sQuery(id+"F21.wireOp",EDGE,"E102"),sQuery(id+"F21.wireOp",EDGE,"E103"),sQuery(id+"F21.wireOp",EDGE,"E104"),sQuery(id+"F21.wireOp",EDGE,"E105")])],"isStart":true})]});
            var sketch = newSketch(context, id + "F44", { "sketchPlane" : qUnion([Q0])});
            skLineSegment(sketch, "E139", {"start": v(32.13, 20.54) * mm, "end": v(33.08, 23.4) * mm});
            skArc(sketch, "E140", {"start": v(33.08, 23.4) * mm, "mid": v(32.42, 23.28) * mm, "end": v(31.78, 23.15) * mm});
            skLineSegment(sketch, "E141", {"start": v(32.13, 20.54) * mm, "end": v(31.65, 20.7) * mm});
            skArc(sketch, "E142", {"start": v(31.78, 23.15) * mm, "mid": v(30.78, 21.98) * mm, "end": v(31.65, 20.7) * mm});
            skSolve(sketch);
        }
        {
            var Q0;
            Q0=qSketchRegion(id+"F44",true);
            extrude(context, id + "F45", {"entities" : qUnion([Q0]), "operationType" : NewBodyOperationType.REMOVE, "oppositeDirection" : true, "depth" : 25.4 * mm});
        }
        {
            var Q0;
            Q0=makeQuery(id+"F5.opExtrude","CAP_FACE",FACE,{"disambiguationData":[OSD([sQuery(id+"F2.wireOp",EDGE,"E30"),sQuery(id+"F2.wireOp",EDGE,"E31"),sQuery(id+"F2.wireOp",EDGE,"E32"),sQuery(id+"F2.wireOp",EDGE,"E33"),sQuery(id+"F2.wireOp",EDGE,"E34"),sQuery(id+"F2.wireOp",EDGE,"E35"),sQuery(id+"F2.wireOp",EDGE,"E36"),sQuery(id+"F2.wireOp",EDGE,"E37"),sQuery(id+"F2.wireOp",EDGE,"E38"),sQuery(id+"F2.wireOp",EDGE,"E39"),sQuery(id+"F2.wireOp",EDGE,"E40"),sQuery(id+"F2.wireOp",EDGE,"E45"),sQuery(id+"F2.wireOp",EDGE,"E46"),sQuery(id+"F2.wireOp",EDGE,"E47"),sQuery(id+"F2.wireOp",EDGE,"E48"),sQuery(id+"F2.wireOp",EDGE,"E49"),sQuery(id+"F2.wireOp",EDGE,"E50"),sQuery(id+"F2.wireOp",EDGE,"E51"),sQuery(id+"F2.wireOp",EDGE,"E52"),sQuery(id+"F2.wireOp",EDGE,"E53"),sQuery(id+"F2.wireOp",EDGE,"E54"),sQuery(id+"F2.wireOp",EDGE,"E59")])],"isStart":false});
            var sketch = newSketch(context, id + "F46", { "sketchPlane" : qUnion([Q0])});
            skLineSegment(sketch, "E143", {"start": v(53.6, -20.54) * mm, "end": v(54.08, -20.7) * mm});
            skLineSegment(sketch, "E144", {"start": v(53.6, -20.54) * mm, "end": v(52.65, -23.4) * mm});
            skArc(sketch, "E145", {"start": v(53.95, -23.15) * mm, "mid": v(54.94, -21.98) * mm, "end": v(54.08, -20.7) * mm});
            skArc(sketch, "E146", {"start": v(52.65, -23.4) * mm, "mid": v(53.3, -23.28) * mm, "end": v(53.95, -23.15) * mm});
            skSolve(sketch);
        }
        {
            var Q0;
            Q0=qSketchRegion(id+"F46",true);
            extrude(context, id + "F47", {"entities" : qUnion([Q0]), "operationType" : NewBodyOperationType.REMOVE, "oppositeDirection" : true, "depth" : 25.4 * mm});
        }
        {
            var Q0;
            Q0=makeQuery(id+"F6.opExtrude","CAP_FACE",FACE,{"disambiguationData":[OSD([sQuery(id+"F3.wireOp",EDGE,"E60.0"),sQuery(id+"F3.wireOp",EDGE,"E60.1"),sQuery(id+"F3.wireOp",EDGE,"E60.2"),sQuery(id+"F3.wireOp",EDGE,"E60.3"),sQuery(id+"F3.wireOp",EDGE,"E60.4"),sQuery(id+"F3.wireOp",EDGE,"E60.5"),sQuery(id+"F3.wireOp",EDGE,"E60.6"),sQuery(id+"F3.wireOp",EDGE,"E60.7"),sQuery(id+"F3.wireOp",EDGE,"E60.8"),sQuery(id+"F3.wireOp",EDGE,"E61"),sQuery(id+"F3.wireOp",EDGE,"E62"),sQuery(id+"F3.wireOp",EDGE,"E63"),sQuery(id+"F3.wireOp",EDGE,"E64")])],"isStart":false});
            var sketch = newSketch(context, id + "F48", { "sketchPlane" : qUnion([Q0])});
            skLineSegment(sketch, "E147", {"start": v(79.89, 5.16) * mm, "end": v(80.85, 8.05) * mm});
            skLineSegment(sketch, "E148", {"start": v(80.85, 8.05) * mm, "end": v(43.78, 22.68) * mm});
            skArc(sketch, "E149", {"start": v(52.85, 15.74) * mm, "mid": v(48.8, 19.84) * mm, "end": v(43.78, 22.68) * mm});
            skArc(sketch, "E150", {"start": v(52.85, 15.74) * mm, "mid": v(63.63, 7.9) * mm, "end": v(76.96, 7.6) * mm});
            skArc(sketch, "E151", {"start": v(79.89, 5.16) * mm, "mid": v(79.07, 7.15) * mm, "end": v(76.96, 7.6) * mm});
            skSolve(sketch);
        }
        {
            var Q0;
            Q0=qSketchRegion(id+"F48",true);
            extrude(context, id + "F49", {"entities" : qUnion([Q0]), "operationType" : NewBodyOperationType.REMOVE, "endBound" : BoundingType.THROUGH_ALL, "oppositeDirection" : true, "depth" : 25.4 * mm});
        }
        {
            var Q0;
            Q0=makeQuery(id+"F22.boolean.opBoolean","MERGE",FACE,{"derivedFrom":[makeQuery(id+"F4.opExtrude","CAP_FACE",FACE,{"disambiguationData":[OSD([sQuery(id+"F1.wireOp",EDGE,"E0"),sQuery(id+"F1.wireOp",EDGE,"E3"),sQuery(id+"F1.wireOp",EDGE,"E4"),sQuery(id+"F1.wireOp",EDGE,"E5"),sQuery(id+"F1.wireOp",EDGE,"E6"),sQuery(id+"F1.wireOp",EDGE,"E7"),sQuery(id+"F1.wireOp",EDGE,"E8"),sQuery(id+"F1.wireOp",EDGE,"E9"),sQuery(id+"F1.wireOp",EDGE,"E10"),sQuery(id+"F1.wireOp",EDGE,"E11"),sQuery(id+"F1.wireOp",EDGE,"E12"),sQuery(id+"F1.wireOp",EDGE,"E13"),sQuery(id+"F1.wireOp",EDGE,"E17"),sQuery(id+"F1.wireOp",EDGE,"E18"),sQuery(id+"F1.wireOp",EDGE,"E19"),sQuery(id+"F1.wireOp",EDGE,"E20"),sQuery(id+"F1.wireOp",EDGE,"E21"),sQuery(id+"F1.wireOp",EDGE,"E22"),sQuery(id+"F1.wireOp",EDGE,"E23"),sQuery(id+"F1.wireOp",EDGE,"E24"),sQuery(id+"F1.wireOp",EDGE,"E25"),sQuery(id+"F1.wireOp",EDGE,"E26")])],"isStart":false}),makeQuery(id+"F22.opExtrude","CAP_FACE",FACE,{"disambiguationData":[OSD([sQuery(id+"F21.wireOp",EDGE,"E98"),sQuery(id+"F21.wireOp",EDGE,"E99"),sQuery(id+"F21.wireOp",EDGE,"E100"),sQuery(id+"F21.wireOp",EDGE,"E101")])],"isStart":true}),makeQuery(id+"F22.opExtrude","CAP_FACE",FACE,{"disambiguationData":[OSD([sQuery(id+"F21.wireOp",EDGE,"E102"),sQuery(id+"F21.wireOp",EDGE,"E103"),sQuery(id+"F21.wireOp",EDGE,"E104"),sQuery(id+"F21.wireOp",EDGE,"E105")])],"isStart":true})]});
            var sketch = newSketch(context, id + "F50", { "sketchPlane" : qUnion([Q0])});
            skLineSegment(sketch, "E152", {"start": v(7.23, 26.17) * mm, "end": v(6.67, 24.48) * mm});
            skLineSegment(sketch, "E153", {"start": v(6.67, 24.48) * mm, "end": v(30.76, 16.45) * mm});
            skLineSegment(sketch, "E154", {"start": v(30.76, 16.45) * mm, "end": v(31.33, 18.13) * mm});
            skLineSegment(sketch, "E155", {"start": v(31.33, 18.13) * mm, "end": v(7.23, 26.17) * mm});
            skLineSegment(sketch, "E156", {"start": v(77.93, 0.72) * mm, "end": v(85.73, -1.87) * mm});
            skLineSegment(sketch, "E157", {"start": v(85.73, -1.87) * mm, "end": v(85.73, 0) * mm});
            skLineSegment(sketch, "E158", {"start": v(85.73, 0) * mm, "end": v(78.5, 2.4) * mm});
            skLineSegment(sketch, "E159", {"start": v(78.5, 2.4) * mm, "end": v(77.93, 0.72) * mm});
            skSolve(sketch);
        }
        {
            var Q0;
            Q0=qSketchRegion(id+"F50",true);
            extrude(context, id + "F51", {"entities" : qUnion([Q0]), "operationType" : NewBodyOperationType.REMOVE, "endBound" : BoundingType.THROUGH_ALL, "oppositeDirection" : true, "depth" : 25.4 * mm});
        }
        {
            var Q0;
            Q0=makeQuery(id+"F5.opExtrude","CAP_FACE",FACE,{"disambiguationData":[OSD([sQuery(id+"F2.wireOp",EDGE,"E30"),sQuery(id+"F2.wireOp",EDGE,"E31"),sQuery(id+"F2.wireOp",EDGE,"E32"),sQuery(id+"F2.wireOp",EDGE,"E33"),sQuery(id+"F2.wireOp",EDGE,"E34"),sQuery(id+"F2.wireOp",EDGE,"E35"),sQuery(id+"F2.wireOp",EDGE,"E36"),sQuery(id+"F2.wireOp",EDGE,"E37"),sQuery(id+"F2.wireOp",EDGE,"E38"),sQuery(id+"F2.wireOp",EDGE,"E39"),sQuery(id+"F2.wireOp",EDGE,"E40"),sQuery(id+"F2.wireOp",EDGE,"E45"),sQuery(id+"F2.wireOp",EDGE,"E46"),sQuery(id+"F2.wireOp",EDGE,"E47"),sQuery(id+"F2.wireOp",EDGE,"E48"),sQuery(id+"F2.wireOp",EDGE,"E49"),sQuery(id+"F2.wireOp",EDGE,"E50"),sQuery(id+"F2.wireOp",EDGE,"E51"),sQuery(id+"F2.wireOp",EDGE,"E52"),sQuery(id+"F2.wireOp",EDGE,"E53"),sQuery(id+"F2.wireOp",EDGE,"E54"),sQuery(id+"F2.wireOp",EDGE,"E59")])],"isStart":false});
            var sketch = newSketch(context, id + "F52", { "sketchPlane" : qUnion([Q0])});
            skLineSegment(sketch, "E160", {"start": v(0, 0) * mm, "end": v(0, 1.87) * mm});
            skLineSegment(sketch, "E161", {"start": v(0, 1.87) * mm, "end": v(7.8, -0.72) * mm});
            skLineSegment(sketch, "E162", {"start": v(7.8, -0.72) * mm, "end": v(7.23, -2.4) * mm});
            skLineSegment(sketch, "E163", {"start": v(7.23, -2.4) * mm, "end": v(0, 0) * mm});
            skLineSegment(sketch, "E164", {"start": v(54.4, -18.13) * mm, "end": v(54.96, -16.45) * mm});
            skLineSegment(sketch, "E165", {"start": v(54.96, -16.45) * mm, "end": v(79.06, -24.48) * mm});
            skLineSegment(sketch, "E166", {"start": v(79.06, -24.48) * mm, "end": v(78.5, -26.17) * mm});
            skLineSegment(sketch, "E167", {"start": v(78.5, -26.17) * mm, "end": v(54.4, -18.13) * mm});
            skSolve(sketch);
        }
        {
            var Q0;
            Q0=qSketchRegion(id+"F52",true);
            extrude(context, id + "F53", {"entities" : qUnion([Q0]), "operationType" : NewBodyOperationType.REMOVE, "endBound" : BoundingType.THROUGH_ALL, "oppositeDirection" : true, "depth" : 25.4 * mm});
        }
    });
